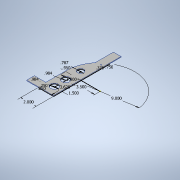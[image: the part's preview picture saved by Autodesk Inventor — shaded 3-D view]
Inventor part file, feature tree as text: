
AUTODESK INVENTOR PART (.ipt)
format: ipt  version: 2021 (Build 250183000, 183)  size: 147,456 bytes
history: native  units: in
note: dims shown in document units (in); Inventor stores cm internally (conversion verified against a paired STEP export)
features: sketch x2, extrude x2, hole x1
ambient origin geometry x8: Origin, YZ Plane, XZ Plane, XY Plane, X Axis, Y Axis, Z Axis, Center Point
bodies: Solid1 (feature_tree)
feature tree (5):
  sketch  "Sketch1"  dims[d0=9.0in d1=3.62in]
  extrude  "Extrusion1"  Depth=3.62in
  hole  "Hole1"  [1 undecoded]
  extrude  "Extrusion2"  Depth=0.09in
  sketch  "Sketch2"  dims[d2=2.0in d3=3.5in d4=0.95in d5=0.7874in d6=1.0in d7=0.984in d8=1.5in d9=0.984in d10=0.09in d11=0.0in d12=0.25in d13=0.25in d14=0.75in d15=0.375in d16=0.129in d17=0.75in d18=0.225in d19=0.25in d20=0.5635in d21=1.0in d22=0.8108in d23=1.5in d24=1.0in d25=1.0in d26=1.0in d27=1.5in d28=1.25in d29=1.25in d30=1.25in d32=0.09in d33=0.0in]
note: 1 required parameter value undecoded (feature->parameter linkage not recoverable at this tier; creation-order binding heuristic only, values carry confidence <= 0.55)
